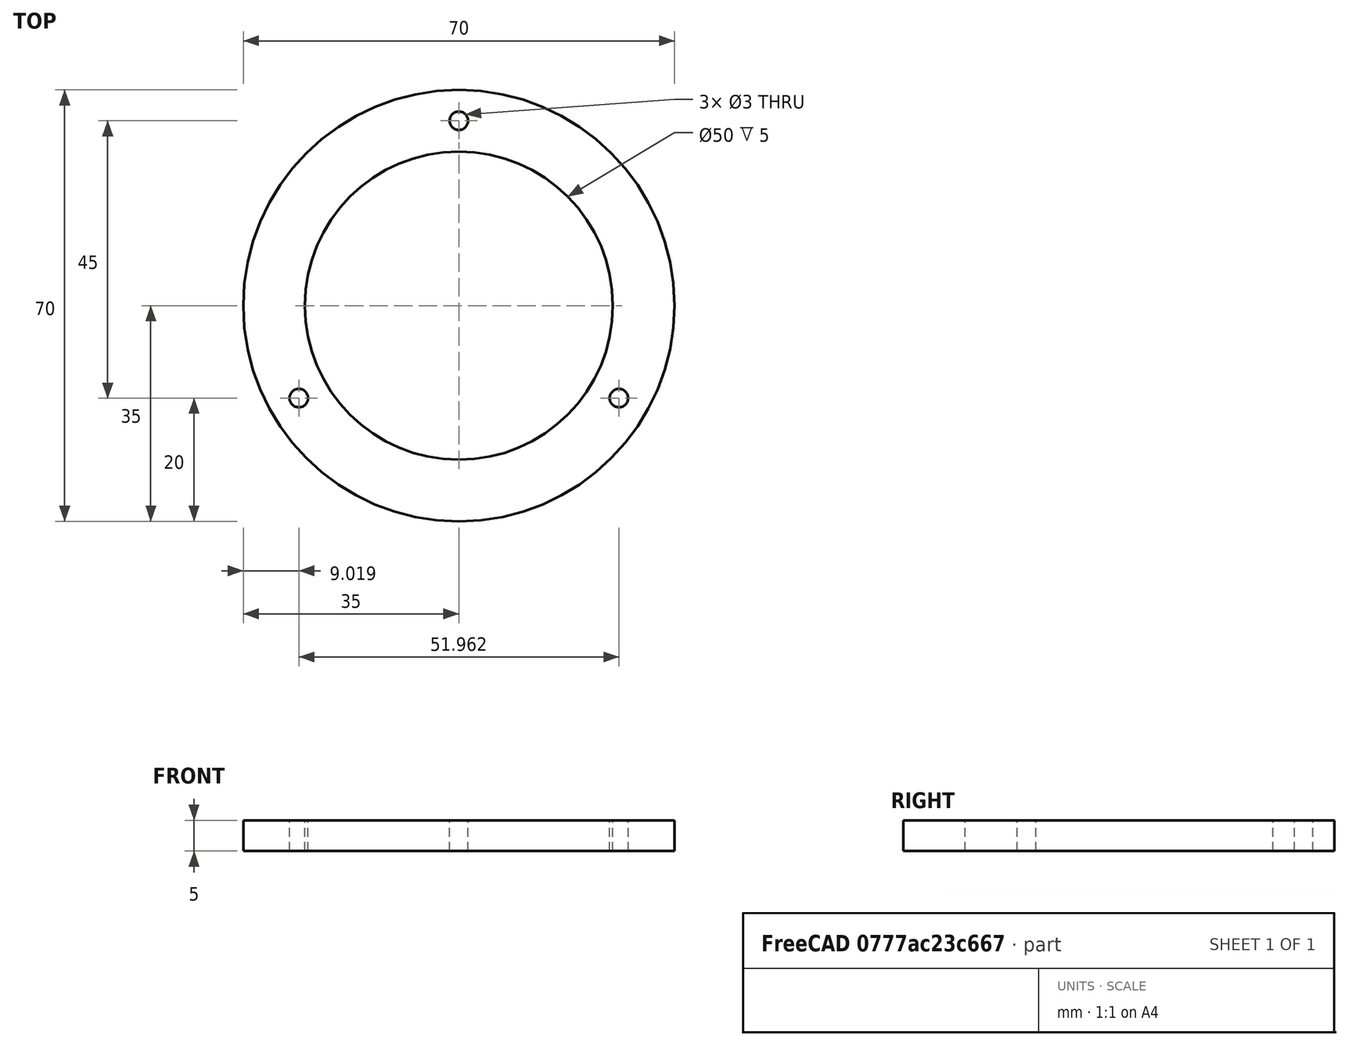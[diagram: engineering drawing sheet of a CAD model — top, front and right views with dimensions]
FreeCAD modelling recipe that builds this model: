
FCSTD DOCUMENT  (FreeCAD 0.16RUnknown)
Label: Art1BotP2
License: All rights reserved
LicenseURL: http://en.wikipedia.org/wiki/All_rights_reserved
objects: Part::Cylinder×3, Part::FeaturePython×1, Part::MultiFuse×1, Part::Cut×1
note: 6 computed .brp shape members not serialized (recipe doc carries the construction recipe); baked Part::Feature solids carry a one-line shape summary decoded from their .brp

FEATURE [Part::Cylinder] Cylinder002  label="CylinderBase"
  Angle = 360
  Height = 5
  Radius = 35
FEATURE [Part::Cylinder] Cylinder003  label="M3Holes"
  Angle = 360
  Height = 5
  Placement = pos=(0,30,0) rot=(0,0,1;0rad)
  Radius = 1.5
FEATURE [Part::FeaturePython] Array  # Draft array (typed FeaturePython)
  Angle = 360
  ArrayType = 1
  Axis = (0,0,1)
  Base = -> Cylinder003
  Center = (0,0,0)
  Fuse = false
  IntervalAxis = (0,0,0)
  IntervalX = (1,0,0)
  IntervalY = (0,1,0)
  IntervalZ = (0,0,0)
  NumberPolar = 3
  NumberX = 2
  NumberY = 2
  NumberZ = 1
FEATURE [Part::Cylinder] Cylinder004  label="CylinderBoring"
  Angle = 360
  Height = 5
  Radius = 25
FEATURE [Part::MultiFuse] Fusion145
  Shapes = -> [Array,Cylinder004]
FEATURE [Part::Cut] Cut
  Base = -> Cylinder002
  Tool = -> Fusion145
